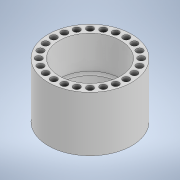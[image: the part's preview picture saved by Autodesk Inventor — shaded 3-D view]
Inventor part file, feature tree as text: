
AUTODESK INVENTOR PART (.ipt)
format: ipt  version: 2020 (Build 240168000, 168)  size: 175,616 bytes
history: native  units: in
note: dims shown in document units (in); Inventor stores cm internally (conversion verified against a paired STEP export)
features: extrude x3, sketch x3, pattern_circular x1, chamfer x1
ambient origin geometry x8: Origin, YZ Plane, XZ Plane, XY Plane, X Axis, Y Axis, Z Axis, Center Point
bodies: Solid1 (feature_tree)
feature tree (8):
  extrude  "Extrusion1"  Depth=1.1024in
  extrude  "Extrusion2"  Depth=0.9843in
  pattern_circular  "Circular Pattern1"  [2 undecoded]
  extrude  "Extrusion3"  Depth=0.3937in TaperAngle=360.0deg
  chamfer  "Chamfer1"  Distance=1.0236in
  sketch  "Sketch1"  dims[d0=1.4961in d1=1.1024in]
  sketch  "Sketch2"  dims[d2=0.9843in d3=0.0in d4=0.1181in]
  sketch  "Sketch3"  dims[d5=0.6496in d6=0.9843in d7=0.0in d8=9.4488in d9=360.0deg d11=1.0236in d12=0.3937in d13=0.0in d14=0.0394in d15=0.0787in d16=45.0deg]
note: 2 required parameter values undecoded (feature->parameter linkage not recoverable at this tier; creation-order binding heuristic only, values carry confidence <= 0.55)
